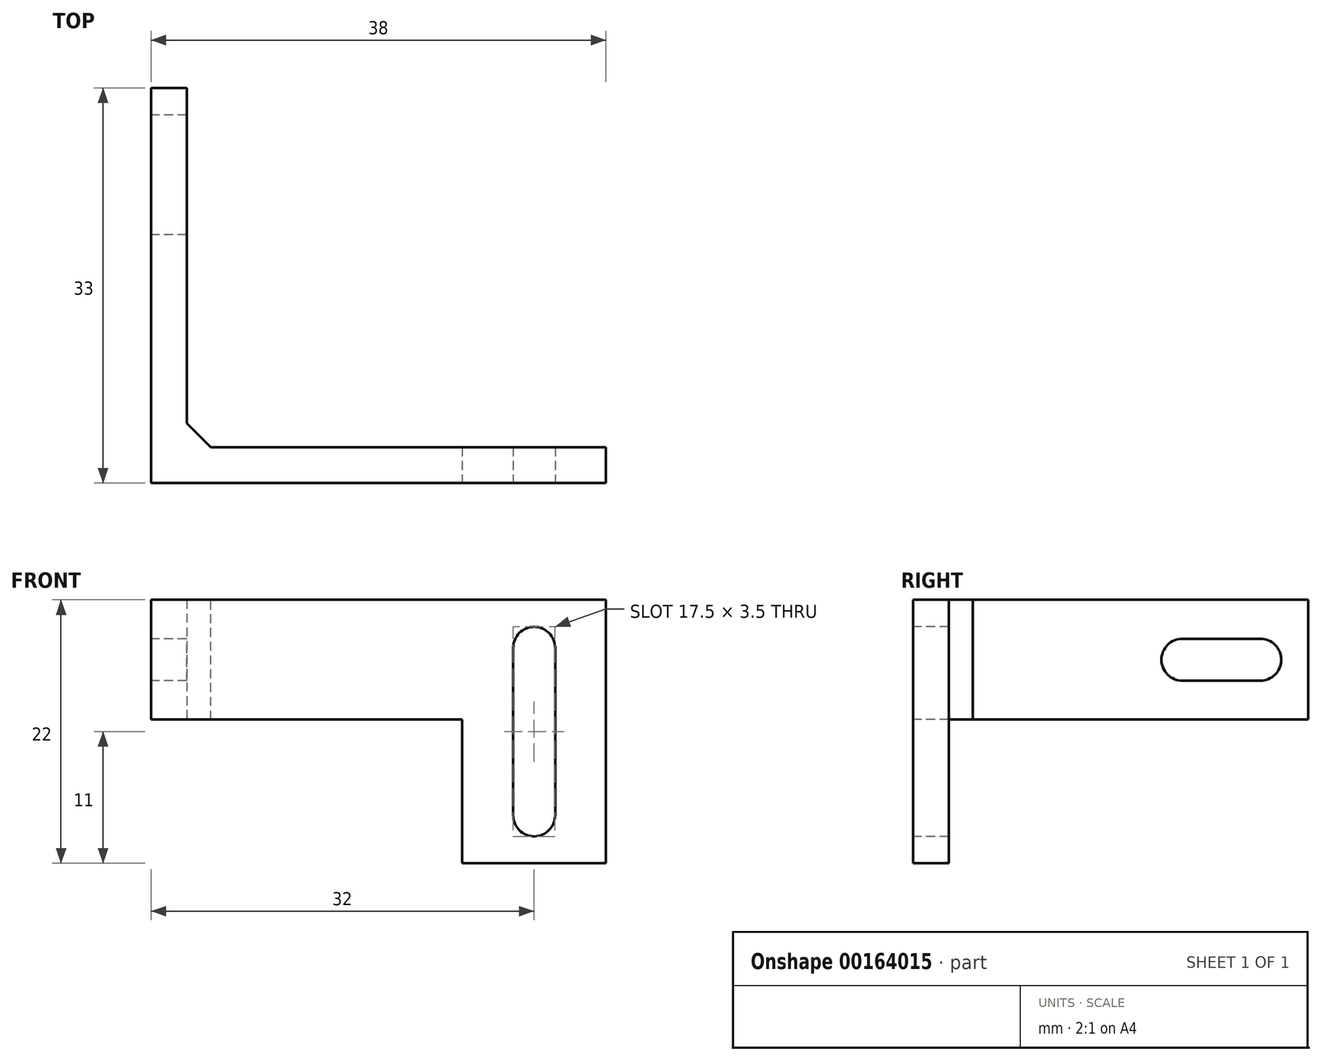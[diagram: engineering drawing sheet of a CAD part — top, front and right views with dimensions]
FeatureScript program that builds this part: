
annotation { "Feature Type Name" : "Feature", "Feature Type Description" : "" }
export const myFeature = defineFeature(function(context is Context, id is Id, definition is map)
    precondition{}
    {
        {
            var Q0;
            Q0=qCreatedBy(makeId("Top.planeOp"),FACE);
            var sketch = newSketch(context, id + "F4", { "sketchPlane" : qUnion([Q0])});
            skLineSegment(sketch, "E0.bottom", {"start": v(-1.5, 0) * mm, "end": v(1.5, 0) * mm});
            skLineSegment(sketch, "E0.top", {"start": v(-1.5, -30) * mm, "end": v(1.5, -30) * mm});
            skLineSegment(sketch, "E0.left", {"start": v(-1.5, 0) * mm, "end": v(-1.5, -30) * mm});
            skLineSegment(sketch, "E0.right", {"start": v(1.5, 0) * mm, "end": v(1.5, -30) * mm});
            skPoint(sketch, "E1", {"position": v(0, 0) * mm});
            skLineSegment(sketch, "E2.bottom", {"start": v(-1.5, -30) * mm, "end": v(36.5, -30) * mm});
            skLineSegment(sketch, "E2.top", {"start": v(-1.5, -33) * mm, "end": v(36.5, -33) * mm});
            skLineSegment(sketch, "E2.left", {"start": v(-1.5, -30) * mm, "end": v(-1.5, -33) * mm});
            skLineSegment(sketch, "E2.right", {"start": v(36.5, -30) * mm, "end": v(36.5, -33) * mm});
            skLineSegment(sketch, "E3", {"start": v(24.5, -30) * mm, "end": v(24.5, -33) * mm});
            skSolve(sketch);
        }
        {
            var Q0;
            Q0=makeQuery(id+"F4.imprint","IMPRINT",FACE,{"disambiguationData":[TD([[makeQuery(id+"F4.imprint","IMPRINT",EDGE,{"derivedFrom":sQuery(id+"F4.wireOp",EDGE,"E0.bottom")}),-1.0]])]});
            var Q1;
            {var subQ0=sQuery(id+"F4.wireOp",EDGE,"E2.left");Q1=makeQuery(id+"F4.imprint","IMPRINT",FACE,{"disambiguationData":[TD([[makeQuery(id+"F4.imprint","IMPRINT",EDGE,{"derivedFrom":subQ0}),1.0]])]});}
            var Q2;
            {var subQ0=sQuery(id+"F4.wireOp",EDGE,"E2.right");Q2=makeQuery(id+"F4.imprint","IMPRINT",FACE,{"disambiguationData":[TD([[makeQuery(id+"F4.imprint","IMPRINT",EDGE,{"derivedFrom":subQ0}),-1.0]])]});}
            extrude(context, id + "F5", {"entities" : qUnion([Q0, Q1, Q2]), "depth" : 10 * mm});
        }
        {
            var Q0;
            {var subQ0=sQuery(id+"F4.wireOp",EDGE,"E2.right");Q0=makeQuery(id+"F4.imprint","IMPRINT",FACE,{"disambiguationData":[TD([[makeQuery(id+"F4.imprint","IMPRINT",EDGE,{"derivedFrom":subQ0}),-1.0]])]});}
            extrude(context, id + "F0", {"entities" : qUnion([Q0]), "operationType" : NewBodyOperationType.ADD, "oppositeDirection" : true, "depth" : 12 * mm});
        }
        {
            var Q0;
            Q0=makeQuery(id+"F5.opExtrude","SWEPT_FACE",FACE,{"disambiguationData":[OSD([sQuery(id+"F4.wireOp",EDGE,"E0.left"),sQuery(id+"F4.wireOp",EDGE,"E2.left")])]});
            var sketch = newSketch(context, id + "F1", { "sketchPlane" : qUnion([Q0])});
            skCircle(sketch, "E4", {"center": v(4, 5) * mm, "radius": 1.75 * mm});
            skCircle(sketch, "E5", {"center": v(10.5, 5) * mm, "radius": 1.75 * mm});
            skLineSegment(sketch, "E6", {"start": v(4, 6.75) * mm, "end": v(4, 3.25) * mm, "construction": true});
            skLineSegment(sketch, "E7", {"start": v(10.5, 6.75) * mm, "end": v(10.5, 3.25) * mm, "construction": true});
            skLineSegment(sketch, "E8", {"start": v(4, 6.75) * mm, "end": v(10.5, 6.75) * mm});
            skLineSegment(sketch, "E9", {"start": v(4, 3.25) * mm, "end": v(10.5, 3.25) * mm});
            skLineSegment(sketch, "E10", {"start": v(4, 6.75) * mm, "end": v(4, 10) * mm, "construction": true});
            skLineSegment(sketch, "E11", {"start": v(4, 3.25) * mm, "end": v(4, 0) * mm, "construction": true});
            skSolve(sketch);
        }
        {
            var Q0;
            {var subQ0=sQuery(id+"F1.wireOp",EDGE,"E4");var subQ1=makeQuery(id+"F1.imprint","INTERSECT",VERTEX,{"derivedFrom":[subQ0,sQuery(id+"F1.wireOp",EDGE,"E8")]});Q0=makeQuery(id+"F1.imprint","IMPRINT",FACE,{"disambiguationData":[TD([[makeQuery(id+"F1.imprint","IMPRINT",EDGE,{"disambiguationData":[TD([[subQ1,-1.0]])],"derivedFrom":subQ0}),1.0]])]});}
            var Q1;
            {var subQ0=sQuery(id+"F1.wireOp",EDGE,"E8");Q1=makeQuery(id+"F1.imprint","IMPRINT",FACE,{"disambiguationData":[TD([[makeQuery(id+"F1.imprint","IMPRINT",EDGE,{"derivedFrom":subQ0}),-1.0]])]});}
            var Q2;
            {var subQ0=sQuery(id+"F1.wireOp",EDGE,"E5");var subQ1=makeQuery(id+"F1.imprint","INTERSECT",VERTEX,{"derivedFrom":[subQ0,sQuery(id+"F1.wireOp",EDGE,"E8")]});Q2=makeQuery(id+"F1.imprint","IMPRINT",FACE,{"disambiguationData":[TD([[makeQuery(id+"F1.imprint","IMPRINT",EDGE,{"disambiguationData":[TD([[subQ1,-1.0]])],"derivedFrom":subQ0}),1.0]])]});}
            extrude(context, id + "F2", {"entities" : qUnion([Q0, Q1, Q2]), "operationType" : NewBodyOperationType.REMOVE, "endBound" : BoundingType.THROUGH_ALL, "oppositeDirection" : true, "depth" : 25 * mm});
        }
        {
            var Q0;
            {var subQ0=sQuery(id+"F4.wireOp",EDGE,"E2.top");Q0=makeQuery(id+"F0.boolean.opBoolean","MERGE",FACE,{"derivedFrom":[makeQuery(id+"F5.opExtrude","SWEPT_FACE",FACE,{"disambiguationData":[OSD([subQ0])]}),makeQuery(id+"F0.opExtrude","SWEPT_FACE",FACE,{"disambiguationData":[OSD([subQ0])]})]});}
            var sketch = newSketch(context, id + "F6", { "sketchPlane" : qUnion([Q0])});
            skCircle(sketch, "E12", {"center": v(30.5, -8) * mm, "radius": 1.75 * mm});
            skCircle(sketch, "E13", {"center": v(30.5, 6) * mm, "radius": 1.75 * mm});
            skPoint(sketch, "E14", {"position": v(30.5, -12) * mm});
            skLineSegment(sketch, "E15", {"start": v(32.25, -8) * mm, "end": v(32.25, 6) * mm});
            skLineSegment(sketch, "E16", {"start": v(28.75, -8) * mm, "end": v(28.75, 6) * mm});
            skLineSegment(sketch, "E17", {"start": v(30.5, -8) * mm, "end": v(36.5, -8) * mm, "construction": true});
            skLineSegment(sketch, "E18", {"start": v(30.5, -8) * mm, "end": v(24.5, -8) * mm, "construction": true});
            skSolve(sketch);
        }
        {
            var Q0;
            {var subQ0=sQuery(id+"F6.wireOp",EDGE,"E13");var subQ1=sQuery(id+"F6.wireOp",EDGE,"E12");var subQ2=makeQuery(id+"F6.imprint","INTERSECT",VERTEX,{"disambiguationData":[OD(0.0)],"derivedFrom":[subQ1,subQ0]});Q0=makeQuery(id+"F6.imprint","IMPRINT",FACE,{"disambiguationData":[TD([[makeQuery(id+"F6.imprint","IMPRINT",EDGE,{"disambiguationData":[TD([[subQ2,-1.0]])],"derivedFrom":subQ1}),-1.0]])]});}
            var Q1;
            {var subQ0=sQuery(id+"F6.wireOp",EDGE,"E15");Q1=makeQuery(id+"F6.imprint","IMPRINT",FACE,{"disambiguationData":[TD([[makeQuery(id+"F6.imprint","IMPRINT",EDGE,{"derivedFrom":subQ0}),1.0]])]});}
            var Q2;
            {var subQ0=sQuery(id+"F6.wireOp",EDGE,"E13");var subQ1=sQuery(id+"F6.wireOp",EDGE,"E12");var subQ2=makeQuery(id+"F6.imprint","INTERSECT",VERTEX,{"disambiguationData":[OD(0.0)],"derivedFrom":[subQ1,subQ0]});Q2=makeQuery(id+"F6.imprint","IMPRINT",FACE,{"disambiguationData":[TD([[makeQuery(id+"F6.imprint","IMPRINT",EDGE,{"disambiguationData":[TD([[subQ2,-1.0]])],"derivedFrom":subQ1}),1.0]])]});}
            var Q3;
            {var subQ0=sQuery(id+"F6.wireOp",EDGE,"E16");Q3=makeQuery(id+"F6.imprint","IMPRINT",FACE,{"disambiguationData":[TD([[makeQuery(id+"F6.imprint","IMPRINT",EDGE,{"derivedFrom":subQ0}),-1.0]])]});}
            var Q4;
            {var subQ0=sQuery(id+"F6.wireOp",EDGE,"E12");var subQ1=makeQuery(id+"F6.imprint","INTERSECT",VERTEX,{"derivedFrom":[subQ0,sQuery(id+"F6.wireOp",EDGE,"E15")]});Q4=makeQuery(id+"F6.imprint","IMPRINT",FACE,{"disambiguationData":[TD([[makeQuery(id+"F6.imprint","IMPRINT",EDGE,{"disambiguationData":[TD([[subQ1,-1.0]])],"derivedFrom":subQ0}),1.0]])]});}
            var Q5;
            {var subQ0=sQuery(id+"F6.wireOp",EDGE,"E13");var subQ1=makeQuery(id+"F6.imprint","INTERSECT",VERTEX,{"derivedFrom":[subQ0,sQuery(id+"F6.wireOp",EDGE,"E15")]});Q5=makeQuery(id+"F6.imprint","IMPRINT",FACE,{"disambiguationData":[TD([[makeQuery(id+"F6.imprint","IMPRINT",EDGE,{"disambiguationData":[TD([[subQ1,-1.0]])],"derivedFrom":subQ0}),1.0]])]});}
            extrude(context, id + "F7", {"entities" : qUnion([Q0, Q1, Q2, Q3, Q4, Q5]), "operationType" : NewBodyOperationType.REMOVE, "endBound" : BoundingType.THROUGH_ALL, "oppositeDirection" : true, "depth" : 25 * mm});
        }
        {
            var Q0;
            Q0=makeQuery(id+"F5.opExtrude","SWEPT_EDGE",EDGE,{"disambiguationData":[OSD([sQuery(id+"F4.wireOp",EDGE,"E0.right"),sQuery(id+"F4.wireOp",EDGE,"E2.bottom")])]});
            var Q1;
            Q1=makeQuery(id+"F0.opExtrude","CAP_EDGE",EDGE,{"disambiguationData":[OSD([sQuery(id+"F4.wireOp",EDGE,"E3")])],"isStart":true});
            chamfer(context, id + "F3", {"entities" : qUnion([Q0, Q1]), "width" : 2 * mm, "tangentPropagation" : true});
        }
    });
